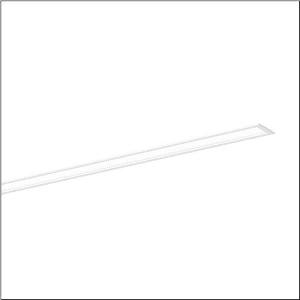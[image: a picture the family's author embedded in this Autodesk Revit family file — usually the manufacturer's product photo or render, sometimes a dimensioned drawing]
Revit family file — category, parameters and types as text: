
# Revit family: silica_r__21_51mx13tctaw_ab10
name_source: partatom
category: Lighting Fixtures
units: mm (PartAtom-declared; Revit-internal decimal feet)

## family parameters
Cut with Voids When Loaded = No
Host = Face
Light Source = No
Part Type = Normal
Room Calculation Point = No
Round Connector Dimension = Use Diameter
Shared = No

## types (1)
- --- (1 x LED, 8070 lm, 81.1 W, 6500K)
    Apparent Load = 81 VA
    CIE Flux Codes = 78 96 99 100 100
    Color Rendering = 80
    Color Temperature = 6500K
    Default Elevation = 1800 mm
    Description = Silica® 21, office luminaire, primary optical cover: prismatic diffuser, of PMMA, CAT 2 (L<= 3000cd/m²), light emission: direct distribution, primary light characteristic: symmetric, installation type: recessed, LED, rated luminous flux: 8.070lm, luminous efficacy: 95lm/W, light colour: 8tw, colour temperature: 2700..6500K, with terminal, 3+2-pole, max. 2.5mm², mains connection: 220..240V, AC, 50/60Hz, rated input power: 85.1W, luminaire housing, of aluminium, traffic white (RAL 9016), length: 3.028mm, width: 79mm, height: 53mm, protection rating (complete): IP20, insulation class (complete): insulation class I (protective earthing), certification: CE, permissible operating ambient temperature: 0..+35°C, standard: EN 50419, packaging unit: 1 piece
    Height = 0 mm  [stored 0 ft]
    Lamp = 1 x LED
    Lamp Light Flux = 8070 lm
    Lamp Power = 81.1 W
    Lamp count = 1
    Length = 3027 mm
    Luminous efficacy = 100 lm/W
    Manufacturer = Siteco
    ModVariant = No
    Model = 51MX13TCTAW
    Mounting Place = Ceiling
    Mounting Type = Recessed
    Number of Poles = 1
    OnlyDefault = Yes
    Power Factor = 1
    Product Name = Silica® 21
    Product group = office luminaire | ceiling recessed
    ProductGroupID = 401
    Protection Class = Protection class I
    Protection Degree = IP 20
    RLX_Detail_Level = 1
    RLX_Emergency_Light_Flux = 0 lm
    RLX_Emergency_Type = 0
    RLX_Emergency_Type_DB = No
    RlxData = <blob elided: 13029 chars, md5=dacac239>
    Socket = socket
    Standby Power = 0 W
    System Light Flux = 8070 lm
    System Power = 81 W
    Type Comments = individual setting
    Type Image = l_1297733.jpg
    URL = http://relux.com
    VarID = @adj_071167
    Voltage = 0 V
    Weight = 0.00 kg
    Width = 79 mm

note: [stored X ft] marks values corroborated as IEEE doubles in the binary element streams (Revit-internal decimal feet)

## geometry (parser evidence)
native form markers: Sweep x10
no freeform markers — native parametric forms only
